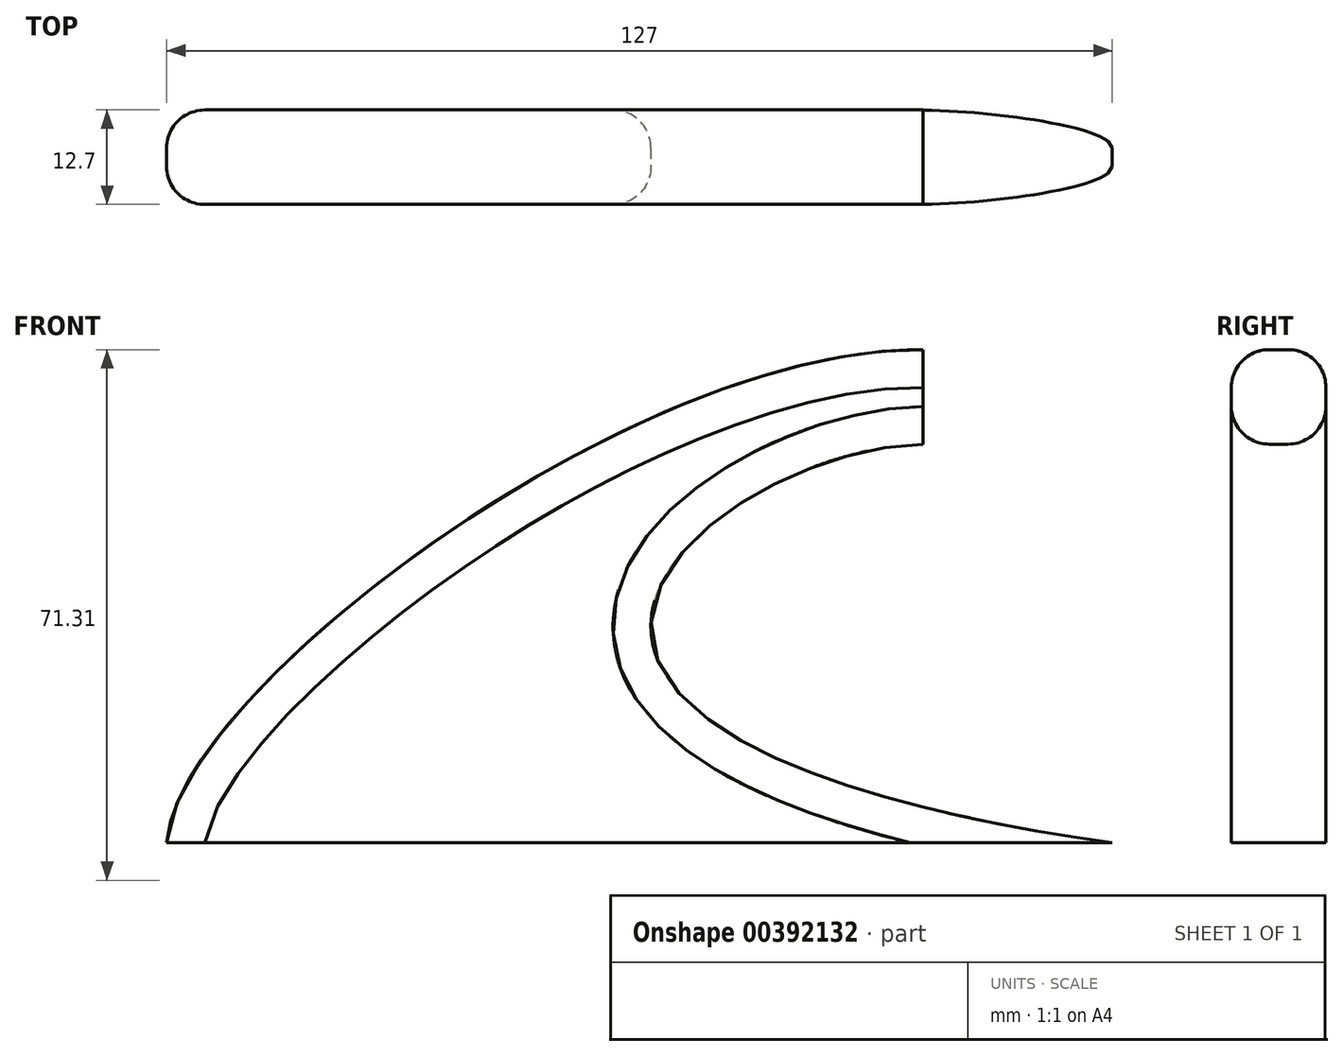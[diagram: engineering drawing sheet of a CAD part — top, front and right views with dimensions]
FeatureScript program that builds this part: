
annotation { "Feature Type Name" : "Feature", "Feature Type Description" : "" }
export const myFeature = defineFeature(function(context is Context, id is Id, definition is map)
    precondition{}
    {
        {
            var Q0;
            Q0=qCreatedBy(makeId("Front.planeOp"),FACE);
            var sketch = newSketch(context, id + "F0", { "sketchPlane" : qUnion([Q0])});
            skLineSegment(sketch, "E0.bottom", {"start": v(63.5, 6.35) * mm, "end": v(-63.5, 6.35) * mm});
            skLineSegment(sketch, "E0.top", {"start": v(63.5, -6.35) * mm, "end": v(-63.5, -6.35) * mm});
            skLineSegment(sketch, "E0.left", {"start": v(63.5, 6.35) * mm, "end": v(63.5, -6.35) * mm});
            skLineSegment(sketch, "E0.right", {"start": v(-63.5, 6.35) * mm, "end": v(-63.5, -6.35) * mm});
            skPoint(sketch, "E0.middle", {"position": v(0, 0) * mm});
            skFitSpline(sketch, "E1", {"points": [v(-63.5, 6.35) * mm, v(38.1, 72.63) * mm], "startDerivative": vector(3.46, 60.2) * mm, "endDerivative": vector(118.3, -0.97) * mm});
            skFitSpline(sketch, "E2", {"points": [v(63.5, 6.35) * mm, v(38.1, 59.93) * mm], "startDerivative": vector(-306.9, 43.9) * mm, "endDerivative": vector(84.24, 1.81) * mm});
            skLineSegment(sketch, "E3", {"start": v(38.1, 72.63) * mm, "end": v(38.1, 59.93) * mm});
            skSolve(sketch);
        }
        {
            var Q0;
            Q0=makeQuery(id+"F0.imprint","IMPRINT",FACE,{"disambiguationData":[TD([[makeQuery(id+"F0.imprint","IMPRINT",EDGE,{"derivedFrom":sQuery(id+"F0.wireOp",EDGE,"E0.bottom")}),-1.0]])]});
            extrude(context, id + "F1", {"entities" : qUnion([Q0]), "endBound" : BoundingType.SYMMETRIC, "depth" : 12.7 * mm});
        }
        {
            var Q0;
            Q0=makeQuery(id+"F1.opExtrude","CAP_EDGE",EDGE,{"disambiguationData":[OSD([sQuery(id+"F0.wireOp",EDGE,"E1")])],"isStart":false});
            var Q1;
            Q1=makeQuery(id+"F1.opExtrude","CAP_EDGE",EDGE,{"disambiguationData":[OSD([sQuery(id+"F0.wireOp",EDGE,"E1")])],"isStart":true});
            var Q2;
            Q2=makeQuery(id+"F1.opExtrude","CAP_EDGE",EDGE,{"disambiguationData":[OSD([sQuery(id+"F0.wireOp",EDGE,"E2")])],"isStart":true});
            var Q3;
            Q3=makeQuery(id+"F1.opExtrude","CAP_EDGE",EDGE,{"disambiguationData":[OSD([sQuery(id+"F0.wireOp",EDGE,"E2")])],"isStart":false});
            fillet(context, id + "F2", {"entities" : qUnion([Q0, Q1, Q2, Q3]), "radius" : 5.08 * mm, "tangentPropagation" : true, "allowEdgeOverflow" : false});
        }
    });
